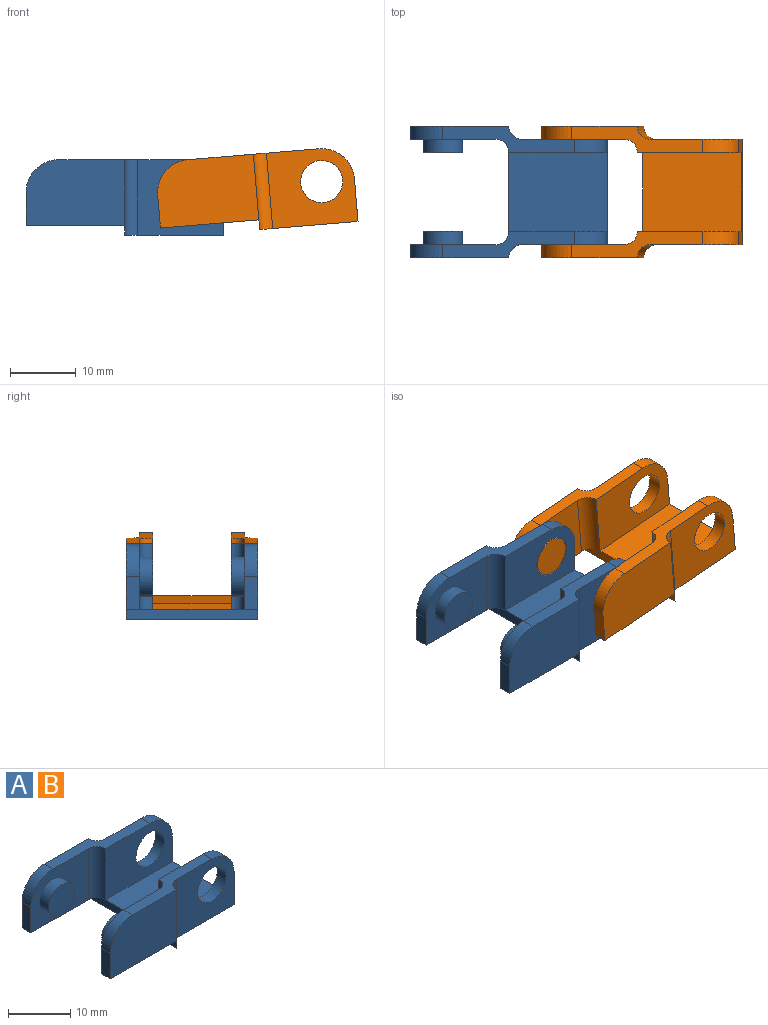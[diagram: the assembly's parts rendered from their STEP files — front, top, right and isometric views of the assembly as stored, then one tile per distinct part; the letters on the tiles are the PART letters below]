
ASSEMBLY  parts=2 mates=1
PART A: 32 faces, bbox 30x20x11.5 mm
  f0: plane 15x4mm, normal (0,0,-1), area 30.9mm2, adj f1,f4,f5,f14,f17
  f1: plane 13x10mm, normal (0,1,0), area 96.4mm2, adj f0,f2,f3,f4,f6,f14
  f2: plane 20x4mm, normal (0,0,1), area 41.7mm2, adj f1,f3,f5,f8,f11,f12,f13,f14
  f3: cylinder r=5mm len=5mm, axis (0,-1,0), area 15.7mm2, adj f1,f2,f4,f5
  f4: plane 5x2mm, normal (-1,0,0), area 10mm2, adj f0,f1,f3,f5
  f5: plane 15x10mm, normal (0,-1,0), area 144.6mm2, adj f0,f2,f3,f4,f13
  f6: cylinder r=3mm len=6mm, axis (0,-1,0), area 37.7mm2, adj f1,f7
  f7: plane 6x6mm, normal (0,1,0), area 28.3mm2, adj f6
  f8: cylinder r=5mm len=5mm, axis (0,-1,0), area 15.7mm2, adj f2,f9,f11,f12
  f9: plane 16x6.5mm, normal (1,0,0), area 44mm2, adj f8,f11,f12,f15,f16,f26,f28,f29
  f10: cylinder r=3.2mm len=6.4mm, axis (0,-1,0), area 40.2mm2, adj f11,f12
  f11: plane 15x10mm, normal (0,1,0), area 112.5mm2, adj f2,f8,f9,f10,f14,f15
  f12: plane 13x11.5mm, normal (0,-1,0), area 112mm2, adj f2,f8,f9,f10,f13,f16
  f13: cylinder r=2mm len=11.5mm, axis (0,0,1), area 36.1mm2, adj f2,f5,f12,f16,f17
  f14: cylinder r=2mm len=10mm, axis (0,0,1), area 31.4mm2, adj f0,f1,f2,f11
  f15: plane 15x12mm, normal (0,0,1), area 180mm2, adj f9,f11,f17,f28
  f16: plane 20x15mm, normal (0,0,-1), area 241.7mm2, adj f9,f12,f13,f17,f29,f30
  f17: plane 20x1.5mm, normal (-1,0,0), area 30mm2, adj f0,f13,f15,f16,f18,f30
  f18: plane 15x4mm, normal (0,0,-1), area 30.9mm2, adj f17,f19,f22,f23,f31
  f19: plane 13x10mm, normal (0,-1,0), area 96.4mm2, adj f18,f20,f21,f22,f24,f31
  f20: plane 20x4mm, normal (0,0,1), area 41.7mm2, adj f19,f21,f23,f26,f28,f29,f30,f31
  f21: cylinder r=5mm len=5mm, axis (0,1,0), area 15.7mm2, adj f19,f20,f22,f23
  f22: plane 5x2mm, normal (-1,0,0), area 10mm2, adj f18,f19,f21,f23
  f23: plane 15x10mm, normal (0,1,0), area 144.6mm2, adj f18,f20,f21,f22,f30
  f24: cylinder r=3mm len=6mm, axis (0,1,0), area 37.7mm2, adj f19,f25
  f25: plane 6x6mm, normal (0,-1,0), area 28.3mm2, adj f24
  f26: cylinder r=5mm len=5mm, axis (0,1,0), area 15.7mm2, adj f9,f20,f28,f29
  f27: cylinder r=3.2mm len=6.4mm, axis (0,1,0), area 40.2mm2, adj f28,f29
  f28: plane 15x10mm, normal (0,-1,0), area 112.5mm2, adj f9,f15,f20,f26,f27,f31
  f29: plane 13x11.5mm, normal (0,1,0), area 112mm2, adj f9,f16,f20,f26,f27,f30
  f30: cylinder r=2mm len=11.5mm, axis (0,0,1), area 36.1mm2, adj f16,f17,f20,f23,f29
  f31: cylinder r=2mm len=10mm, axis (0,0,1), area 31.4mm2, adj f18,f19,f20,f28
PART B: same geometry as A
PLACE A t=(-16.98,2.4,1.07)mm fixed
PLACE B rot(axis=(0,-1,0),4.8deg) t=(3.45,2.4,0.67)mm
MATE revolute B.f3 <-> A.f8  axis (0,1,0) through (8.02,10.4,6.07)mm
